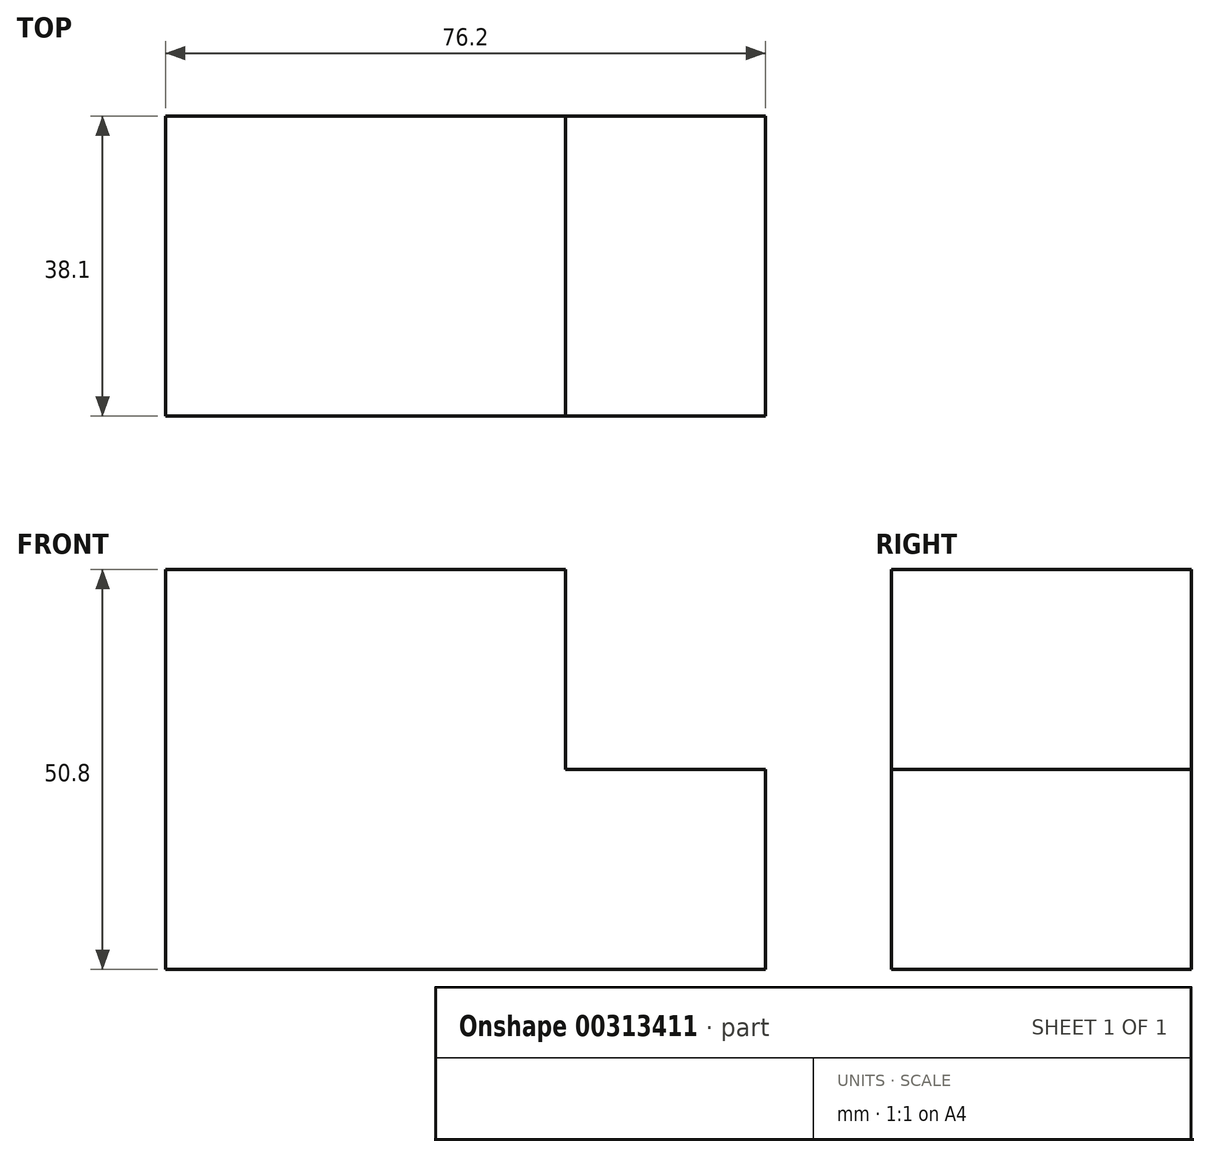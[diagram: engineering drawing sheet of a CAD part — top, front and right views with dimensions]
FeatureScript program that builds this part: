
annotation { "Feature Type Name" : "Feature", "Feature Type Description" : "" }
export const myFeature = defineFeature(function(context is Context, id is Id, definition is map)
    precondition{}
    {
        {
            var Q0;
            Q0=qCreatedBy(makeId("Front.planeOp"),FACE);
            var sketch = newSketch(context, id + "F0", { "sketchPlane" : qUnion([Q0])});
            skLineSegment(sketch, "E0", {"start": v(-33.54, -39.64) * mm, "end": v(42.66, -39.64) * mm});
            skLineSegment(sketch, "E1", {"start": v(42.66, -39.64) * mm, "end": v(42.66, -14.24) * mm});
            skLineSegment(sketch, "E2", {"start": v(42.66, -14.24) * mm, "end": v(17.26, -14.24) * mm});
            skLineSegment(sketch, "E3", {"start": v(17.26, -14.24) * mm, "end": v(17.26, 11.16) * mm});
            skLineSegment(sketch, "E4", {"start": v(17.26, 11.16) * mm, "end": v(-33.54, 11.16) * mm});
            skLineSegment(sketch, "E5", {"start": v(-33.54, 11.16) * mm, "end": v(-33.54, -39.64) * mm});
            skSolve(sketch);
        }
        {
            var Q0;
            Q0=makeQuery(id+"F0.imprint","IMPRINT",FACE,{"disambiguationData":[TD([[makeQuery(id+"F0.imprint","IMPRINT",EDGE,{"derivedFrom":sQuery(id+"F0.wireOp",EDGE,"E0")}),1.0]])]});
            extrude(context, id + "F1", {"entities" : qUnion([Q0]), "depth" : 38.1 * mm});
        }
    });
